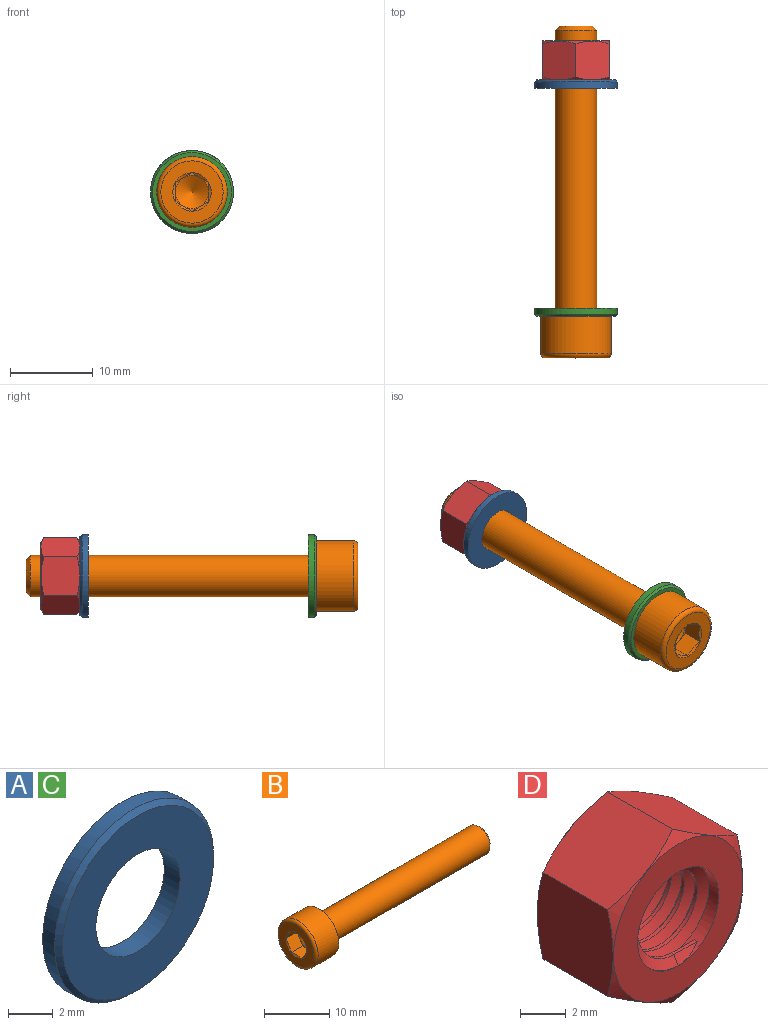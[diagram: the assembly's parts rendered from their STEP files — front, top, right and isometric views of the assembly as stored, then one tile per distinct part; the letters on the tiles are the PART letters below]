
ASSEMBLY  parts=4 mates=3
PART A: 5 faces, bbox 10x1x10 mm
  f0: cylinder r=2.65mm len=5.3mm, axis (0,1,0), area 16.7mm2, adj f2,f3
  f1: cylinder r=5mm len=10mm, axis (0,1,0), area 23.6mm2, adj f3,f4
  f2: plane 9.5x9.5mm, normal (0,-1,0), area 48.8mm2, adj f0,f4
  f3: plane 10x10mm, normal (0,1,0), area 56.5mm2, adj f0,f1
  f4: cone r=5mm half-angle=45deg, axis (0,1,0), area 10.8mm2, adj f1,f2
PART B: 24 faces, bbox 40x9.2x9.2 mm
  f0: plane 1.73x1mm, normal (-1,0,0), area 0.2mm2, adj f16,f17,f23
  f1: plane 2x0.58mm, normal (-1,0,0), area 0.2mm2, adj f17,f18,f23
  f2: plane 1.73x1mm, normal (-1,0,0), area 0.2mm2, adj f18,f19,f23
  f3: plane 1.73x1mm, normal (-1,0,0), area 0.2mm2, adj f19,f20,f23
  f4: plane 2x0.58mm, normal (-1,0,0), area 0.2mm2, adj f20,f21,f23
  f5: cone r=2.31mm half-angle=60deg, axis (-1,0,0), area 3.4mm2, adj f15,f16,f17,f18,f19,f20,f21
  f6: cone r=2.51mm half-angle=20.6deg, axis (-1,0,0), area 6.9mm2, adj f7,f11
  f7: torus R=2.7mm, axis (1,0,0), area 1.1mm2, adj f6,f10
  f8: plane 4.02x4.02mm, normal (1,0,0), area 12.7mm2, adj f9
  f9: cone r=2.5mm half-angle=45deg, axis (-1,0,0), area 9.8mm2, adj f8,f10
  f10: cylinder r=2.5mm len=33.91mm, axis (1,0,0), area 532.6mm2, adj f7,f9
  f11: torus R=2.85mm, axis (1,0,0), area 4.2mm2, adj f6,f13
  f12: cylinder r=4.25mm len=8.5mm, axis (1,0,0), area 120.2mm2, adj f13,f14
  f13: plane 8.5x8.5mm, normal (1,0,0), area 31.2mm2, adj f11,f12
  f14: torus R=3.75mm, axis (1,0,0), area 20.1mm2, adj f12,f15
  f15: plane 7.5x7.5mm, normal (-1,0,0), area 27.4mm2, adj f5,f14
  f16: plane 2.5x2.31mm, normal (0,0,-1), area 5.5mm2, adj f0,f5,f17,f21,f22
  f17: plane 2.5x2mm, normal (0,0.87,-0.5), area 5.5mm2, adj f0,f1,f5,f16,f18
  f18: plane 2.5x2mm, normal (0,0.87,0.5), area 5.5mm2, adj f1,f2,f5,f17,f19
  f19: plane 2.5x2.31mm, normal (0,0,1), area 5.5mm2, adj f2,f3,f5,f18,f20
  f20: plane 2.5x2mm, normal (0,-0.87,0.5), area 5.5mm2, adj f3,f4,f5,f19,f21
  f21: plane 2.5x2mm, normal (0,-0.87,-0.5), area 5.5mm2, adj f4,f5,f16,f20,f22
  f22: plane 1.73x1mm, normal (-1,0,0), area 0.2mm2, adj f16,f21,f23
  f23: cone r=2mm half-angle=60deg, axis (-1,0,0), area 14.5mm2, adj f0,f1,f2,f3,f4,f22
PART C: same geometry as A
PART D: 18 faces, bbox 9.4x4.8x9.4 mm
  f0: plane 7.99x7.99mm, normal (0,-1,0), area 30.5mm2, adj f2,f11
  f1: plane 7.99x7.99mm, normal (0,1,0), area 30.5mm2, adj f2,f10
  f2: cylinder r=2.5mm len=5mm, axis (0,1,0), area 18mm2, adj f0,f1,f3,f5,f6,f7,f8,f9
  f3: plane 0.7x0.46mm, normal (-1,0,-0.03), area 0.2mm2, adj f2,f4,f5,f6
  f4: cylinder r=2.04mm len=4.17mm, axis (0,1,0), area 11.3mm2, adj f3,f5,f6,f7
  f5: bspline ~5.77x5mm, area 37.6mm2, adj f2,f3,f4,f8
  f6: bspline ~5.77x5mm, area 37.6mm2, adj f2,f3,f4,f9
  f7: plane 1.44x0.18mm, normal (0,0,1), area 0.3mm2, adj f2,f4,f8,f9
  f8: plane 1.57x0.59mm, normal (0,0.87,0.5), area 0.5mm2, adj f2,f5,f7
  f9: plane 1.57x0.59mm, normal (0,-0.87,0.5), area 0.5mm2, adj f2,f6,f7
  f10: cone r=3.99mm half-angle=60deg, axis (0,-1,0), area 6.1mm2, adj f1,f12,f13,f14,f15,f16,f17
  f11: cone r=4.62mm half-angle=60deg, axis (0,1,0), area 6.1mm2, adj f0,f12,f13,f14,f15,f16,f17
  f12: plane 4.7x4mm, normal (-0.5,0,0.87), area 20.5mm2, adj f10,f11,f13,f17
  f13: plane 4.7x4mm, normal (0.5,0,0.87), area 20.5mm2, adj f10,f11,f12,f14
  f14: plane 4.69x4.62mm, normal (1,0,0), area 20.5mm2, adj f10,f11,f13,f15
  f15: plane 4.7x4mm, normal (0.5,0,-0.87), area 20.5mm2, adj f10,f11,f14,f16
  f16: plane 4.7x4mm, normal (-0.5,0,-0.87), area 20.5mm2, adj f10,f11,f15,f17
  f17: plane 4.69x4.62mm, normal (-1,0,0), area 20.5mm2, adj f10,f11,f12,f16
PLACE A rot(axis=(1,0,0),180deg) t=(0,26.5,0)mm
PLACE B rot(axis=(-0.58,-0.58,0.58),120deg) t=(0,-1,0)mm
PLACE C at identity fixed
PLACE D t=(0,32.2,0)mm
MATE fastened A.f0 <-> C.f0  axis (0,-1,0) through (0,26.5,0)mm
MATE fastened D.f2 <-> A.f0  axis (0,-1,0) through (0,27.5,0)mm
MATE fastened B.f5 <-> C.f0  axis (0,1,0) through (0,-1,0)mm
